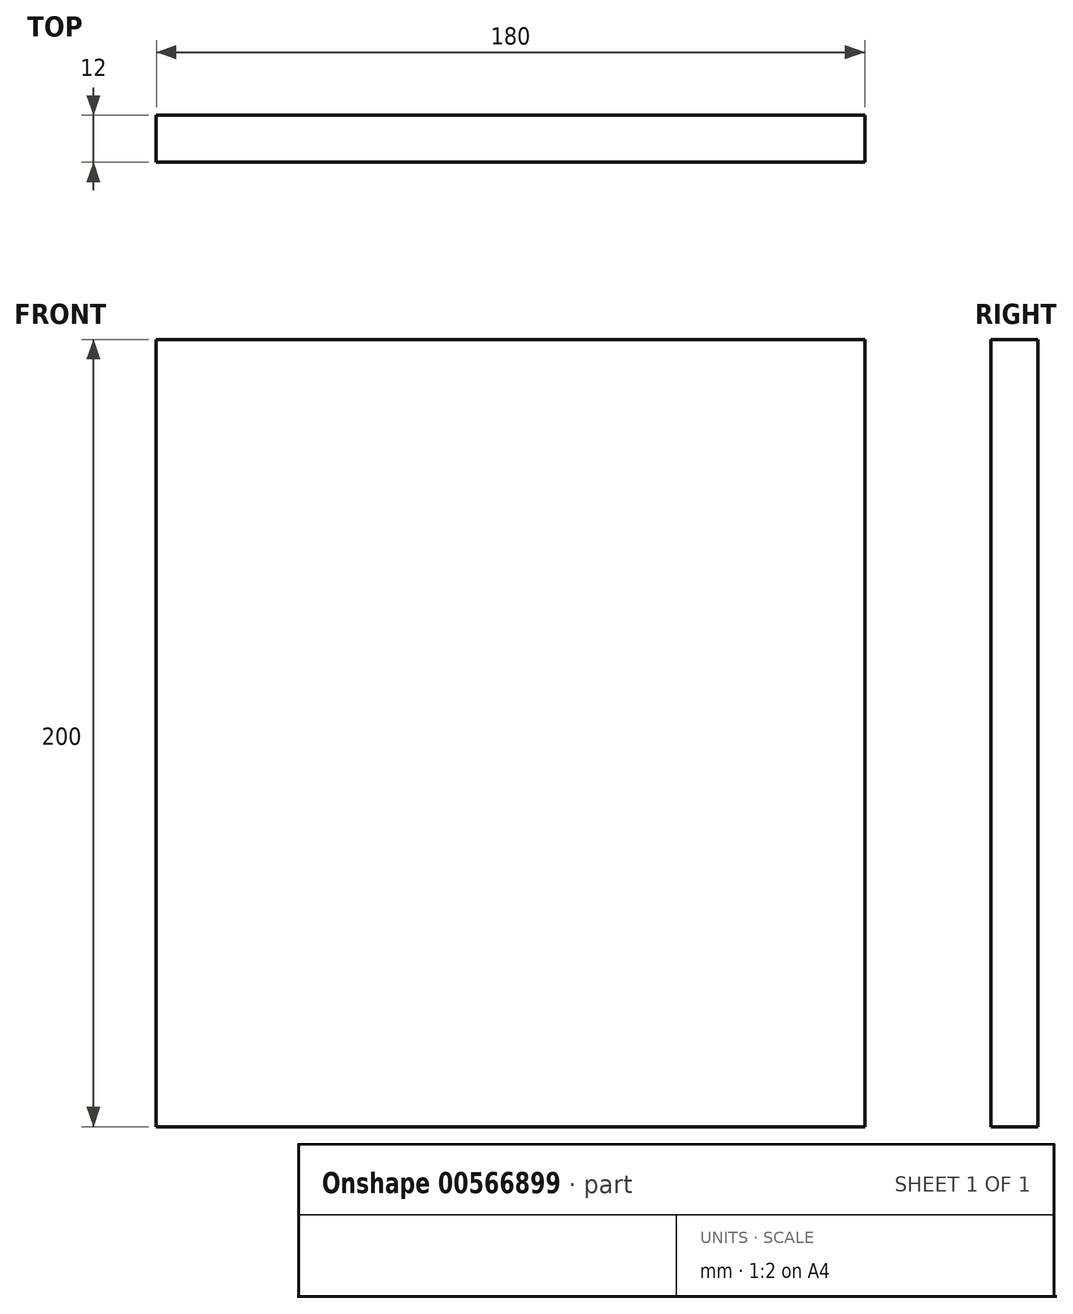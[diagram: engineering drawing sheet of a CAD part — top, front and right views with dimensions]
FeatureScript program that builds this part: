
annotation { "Feature Type Name" : "Feature", "Feature Type Description" : "" }
export const myFeature = defineFeature(function(context is Context, id is Id, definition is map)
    precondition{}
    {
        {
            var Q0;
            Q0=qCreatedBy(makeId("Front.planeOp"),FACE);
            var sketch = newSketch(context, id + "F0", { "sketchPlane" : qUnion([Q0])});
            skLineSegment(sketch, "E0", {"start": v(-52.6, -26.52) * mm, "end": v(127.4, -26.52) * mm});
            skLineSegment(sketch, "E1", {"start": v(-52.6, -26.52) * mm, "end": v(-52.6, 173.48) * mm});
            skLineSegment(sketch, "E2", {"start": v(-52.6, 173.48) * mm, "end": v(127.4, 173.48) * mm});
            skLineSegment(sketch, "E3", {"start": v(127.4, 173.48) * mm, "end": v(127.4, -26.52) * mm});
            skSolve(sketch);
        }
        {
            var Q0;
            Q0=makeQuery(id+"F0.imprint","IMPRINT",FACE,{"disambiguationData":[TD([[makeQuery(id+"F0.imprint","IMPRINT",EDGE,{"derivedFrom":sQuery(id+"F0.wireOp",EDGE,"E0")}),1.0]])]});
            extrude(context, id + "F1", {"entities" : qUnion([Q0]), "depth" : 12 * mm, "offsetDistance" : 25 * mm});
        }
    });
